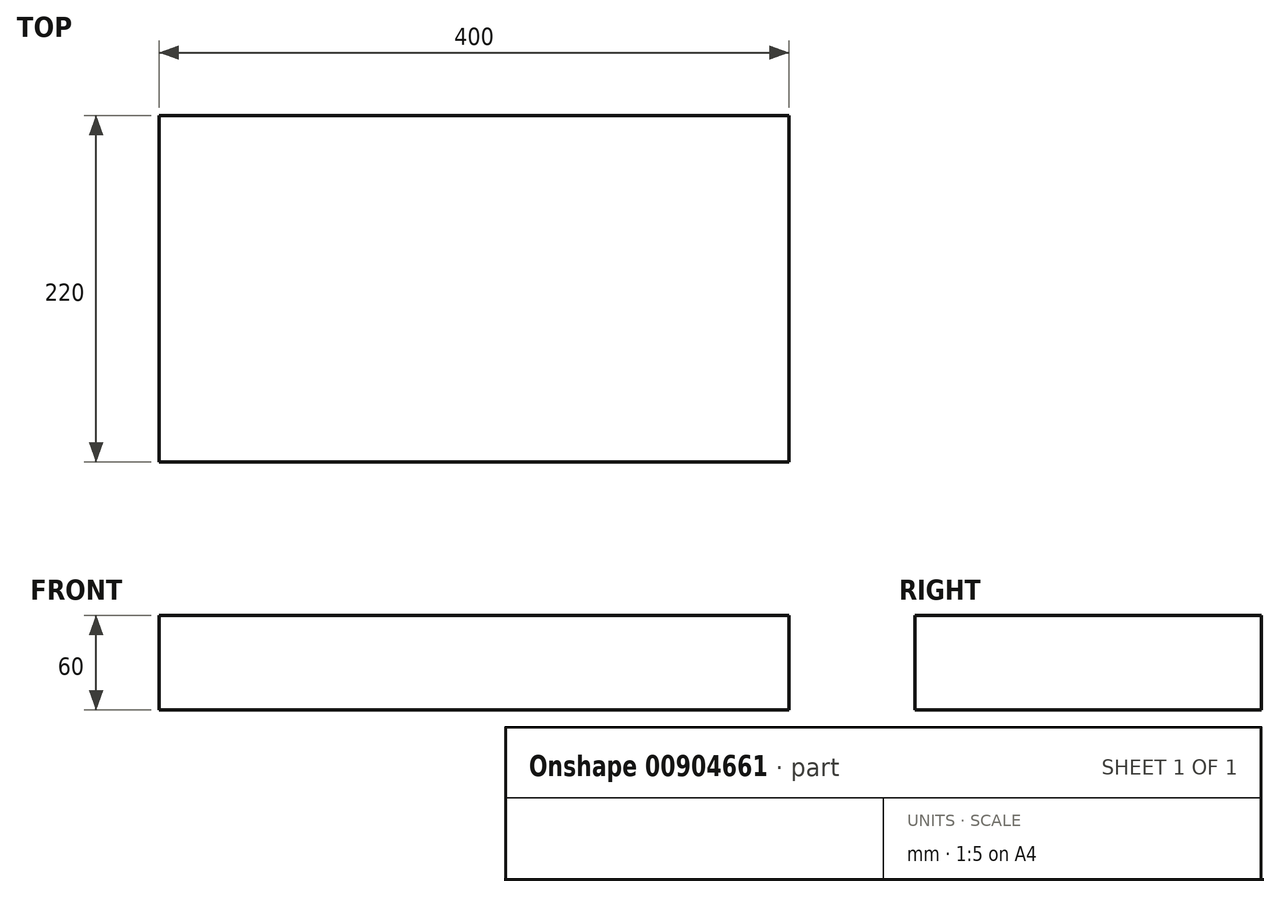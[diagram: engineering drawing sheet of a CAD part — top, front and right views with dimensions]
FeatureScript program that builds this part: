
annotation { "Feature Type Name" : "Feature", "Feature Type Description" : "" }
export const myFeature = defineFeature(function(context is Context, id is Id, definition is map)
    precondition{}
    {
        {
            var Q0;
            Q0=qCreatedBy(makeId("Top.planeOp"),FACE);
            var sketch = newSketch(context, id + "F0", { "sketchPlane" : qUnion([Q0])});
            skLineSegment(sketch, "E0.bottom", {"start": v(0, 0) * mm, "end": v(-400, 0) * mm});
            skLineSegment(sketch, "E0.top", {"start": v(0, 220) * mm, "end": v(-400, 220) * mm});
            skLineSegment(sketch, "E0.left", {"start": v(0, 0) * mm, "end": v(0, 220) * mm});
            skLineSegment(sketch, "E0.right", {"start": v(-400, 0) * mm, "end": v(-400, 220) * mm});
            skSolve(sketch);
        }
        {
            var Q0;
            Q0 = qSketchRegion(id + "F0", true);
            extrude(context, id + "F1", {"entities" : qUnion([Q0]), "depth" : 60 * mm, "offsetDistance" : 25 * mm});
        }
    });
